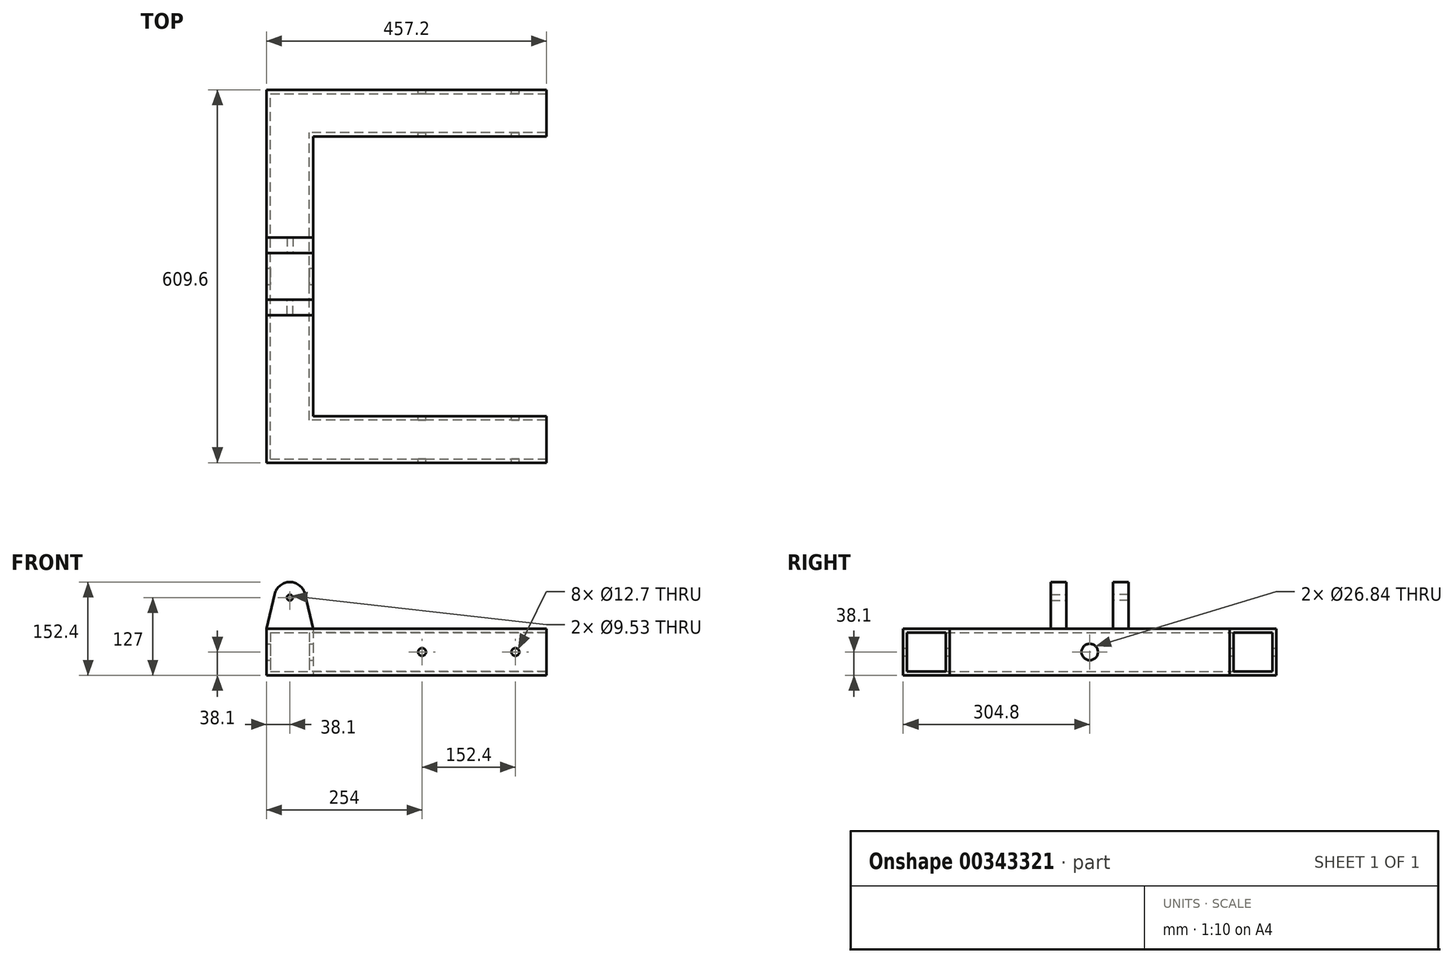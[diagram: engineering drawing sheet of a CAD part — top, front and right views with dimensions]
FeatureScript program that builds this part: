
annotation { "Feature Type Name" : "Feature", "Feature Type Description" : "" }
export const myFeature = defineFeature(function(context is Context, id is Id, definition is map)
    precondition{}
    {
        {
            var Q0;
            Q0=qCreatedBy(makeId("Top.planeOp"),FACE);
            var sketch = newSketch(context, id + "F0", { "sketchPlane" : qUnion([Q0])});
            skLineSegment(sketch, "E0.bottom", {"start": v(-228.6, -304.8) * mm, "end": v(228.6, -304.8) * mm});
            skLineSegment(sketch, "E0.top", {"start": v(-228.6, 304.8) * mm, "end": v(228.6, 304.8) * mm});
            skLineSegment(sketch, "E0.left", {"start": v(-228.6, -304.8) * mm, "end": v(-228.6, 304.8) * mm});
            skLineSegment(sketch, "E0.right", {"start": v(228.6, -304.8) * mm, "end": v(228.6, -228.6) * mm});
            skPoint(sketch, "E0.middle", {"position": v(0, 0) * mm});
            skLineSegment(sketch, "E1.bottom", {"start": v(228.6, -228.6) * mm, "end": v(-152.4, -228.6) * mm});
            skLineSegment(sketch, "E1.top", {"start": v(228.6, 228.6) * mm, "end": v(-152.4, 228.6) * mm});
            skLineSegment(sketch, "E1.right", {"start": v(-152.4, -228.6) * mm, "end": v(-152.4, 228.6) * mm});
            skLineSegment(sketch, "E2.trimOffspring", {"start": v(228.6, 228.6) * mm, "end": v(228.6, 304.8) * mm});
            skSolve(sketch);
        }
        {
            var Q0;
            Q0=makeQuery(id+"F0.imprint","IMPRINT",FACE,{"disambiguationData":[TD([[makeQuery(id+"F0.imprint","IMPRINT",EDGE,{"derivedFrom":sQuery(id+"F0.wireOp",EDGE,"E0.bottom")}),1.0]])]});
            extrude(context, id + "F1", {"entities" : qUnion([Q0]), "depth" : 76.2 * mm});
        }
        {
            var Q0;
            Q0=makeQuery(id+"F1.opExtrude","SWEPT_FACE",FACE,{"disambiguationData":[OSD([sQuery(id+"F0.wireOp",EDGE,"E0.right")])]});
            var Q1;
            Q1=makeQuery(id+"F1.opExtrude","SWEPT_FACE",FACE,{"disambiguationData":[OSD([sQuery(id+"F0.wireOp",EDGE,"E2.trimOffspring")])]});
            shell(context, id + "F2", {"entities" : qUnion([Q0, Q1]), "thickness" : 6.35 * mm});
        }
        {
            var Q0;
            Q0=makeQuery(id+"F1.opExtrude","SWEPT_FACE",FACE,{"disambiguationData":[OSD([sQuery(id+"F0.wireOp",EDGE,"E0.top")])]});
            var sketch = newSketch(context, id + "F3", { "sketchPlane" : qUnion([Q0])});
            skPoint(sketch, "E3", {"position": v(-177.8, 38.1) * mm});
            skPoint(sketch, "E4", {"position": v(-25.4, 38.1) * mm});
            skSolve(sketch);
        }
        {
            var Q0;
            Q0=sQuery(id+"F3.wireOp",VERTEX,"E3");
            var Q1;
            Q1=sQuery(id+"F3.wireOp",VERTEX,"E4");
            var Q2;
            Q2=makeQuery(id+"F1.opExtrude","SWEPT_BODY",BODY,{"disambiguationData":[OSD([sQuery(id+"F0.wireOp",EDGE,"E0.bottom"),sQuery(id+"F0.wireOp",EDGE,"E0.top"),sQuery(id+"F0.wireOp",EDGE,"E0.left"),sQuery(id+"F0.wireOp",EDGE,"E0.right"),sQuery(id+"F0.wireOp",EDGE,"E1.bottom"),sQuery(id+"F0.wireOp",EDGE,"E1.top"),sQuery(id+"F0.wireOp",EDGE,"E1.right"),sQuery(id+"F0.wireOp",EDGE,"E2.trimOffspring")])]});
            hole(context, id + "F4", {"style" : HoleStyle.SIMPLE, "endStyle" : HoleEndStyle.THROUGH, "holeDiameter" : 12.7 * mm, "tappedDepth" : 12.7 * mm, "tapClearance" : 3, "locations" : qUnion([Q0, Q1]), "scope" : qUnion([Q2])});
        }
        {
            var Q0;
            Q0=qCreatedBy(makeId("Front.planeOp"),FACE);
            cPlane(context, id + "F5", {"entities" : qUnion([Q0]), "cplaneType" : CPlaneType.OFFSET, "offset" : 50.8 * mm, "width" : 152.4 * mm, "height" : 152.4 * mm});
        }
        {
            var Q0;
            Q0=qCreatedBy(id+"F5.planeOp",FACE);
            var sketch = newSketch(context, id + "F6", { "sketchPlane" : qUnion([Q0])});
            skLineSegment(sketch, "E5.bottom", {"start": v(-228.6, 76.2) * mm, "end": v(-152.4, 76.2) * mm});
            skLineSegment(sketch, "E5.left", {"start": v(-228.6, 76.2) * mm, "end": v(-215.22, 132.84) * mm});
            skLineSegment(sketch, "E5.right", {"start": v(-152.4, 76.2) * mm, "end": v(-165.78, 132.84) * mm});
            skPoint(sketch, "E6.visualSharp", {"position": v(-190.5, 237.48) * mm});
            skArc(sketch, "E6.filletArc", {"start": v(-165.78, 132.84) * mm, "mid": v(-190.5, 152.4) * mm, "end": v(-215.22, 132.84) * mm});
            skLineSegment(sketch, "E7", {"start": v(-190.5, 76.2) * mm, "end": v(-190.5, 152.4) * mm});
            skCircle(sketch, "E8", {"center": v(-190.5, 127) * mm, "radius": 4.76 * mm});
            skSolve(sketch);
        }
        {
            var Q0;
            {var subQ5=sQuery(id+"F6.wireOp",EDGE,"E5.left");Q0=makeQuery(id+"F6.imprint","IMPRINT",FACE,{"disambiguationData":[TD([[makeQuery(id+"F6.imprint","IMPRINT",EDGE,{"derivedFrom":subQ5}),-1.0]])]});}
            var Q1;
            {var subQ1=sQuery(id+"F6.wireOp",EDGE,"E5.right");Q1=makeQuery(id+"F6.imprint","IMPRINT",FACE,{"disambiguationData":[TD([[makeQuery(id+"F6.imprint","IMPRINT",EDGE,{"derivedFrom":subQ1}),1.0]])]});}
            extrude(context, id + "F7", {"entities" : qUnion([Q0, Q1]), "endBound" : BoundingType.SYMMETRIC, "depth" : 25.4 * mm});
        }
        {
            var Q0;
            Q0=qCreatedBy(makeId("Right.planeOp"),FACE);
            var sketch = newSketch(context, id + "F8", { "sketchPlane" : qUnion([Q0])});
            skCircle(sketch, "E9", {"center": v(0, 38.1) * mm, "radius": 13.42 * mm});
            skSolve(sketch);
        }
        {
            var Q0;
            Q0=makeQuery(id+"F8.imprint","IMPRINT",FACE,{"disambiguationData":[TD([[makeQuery(id+"F8.imprint","IMPRINT",EDGE,{"derivedFrom":sQuery(id+"F8.wireOp",EDGE,"1rv1GFLY-nQxV-duNS-HWr6-cBq558AhsmQw")}),1.0]])]});
            var Q1;
            Q1=makeQuery(id+"F8.imprint","IMPRINT",FACE,{"disambiguationData":[TD([[makeQuery(id+"F8.imprint","IMPRINT",EDGE,{"derivedFrom":sQuery(id+"F8.wireOp",EDGE,"E9")}),1.0]])]});
            extrude(context, id + "F9", {"entities" : qUnion([Q0, Q1]), "operationType" : NewBodyOperationType.REMOVE, "endBound" : BoundingType.THROUGH_ALL, "oppositeDirection" : true, "depth" : 25.4 * mm});
        }
        {
            var Q0;
            Q0=makeQuery(id+"F7.opExtrude","SWEPT_BODY",BODY,{"disambiguationData":[OSD([sQuery(id+"F6.wireOp",EDGE,"E5.bottom"),sQuery(id+"F6.wireOp",EDGE,"E5.left"),sQuery(id+"F6.wireOp",EDGE,"E5.right"),sQuery(id+"F6.wireOp",EDGE,"E6.filletArc"),sQuery(id+"F6.wireOp",EDGE,"E8")])]});
            var Q1;
            Q1=qCreatedBy(makeId("Front.planeOp"),FACE);
            mirror(context, id + "F10", {"operationType" : NewBodyOperationType.ADD, "entities" : qUnion([Q0]), "mirrorPlane" : qUnion([Q1])});
        }
    });
